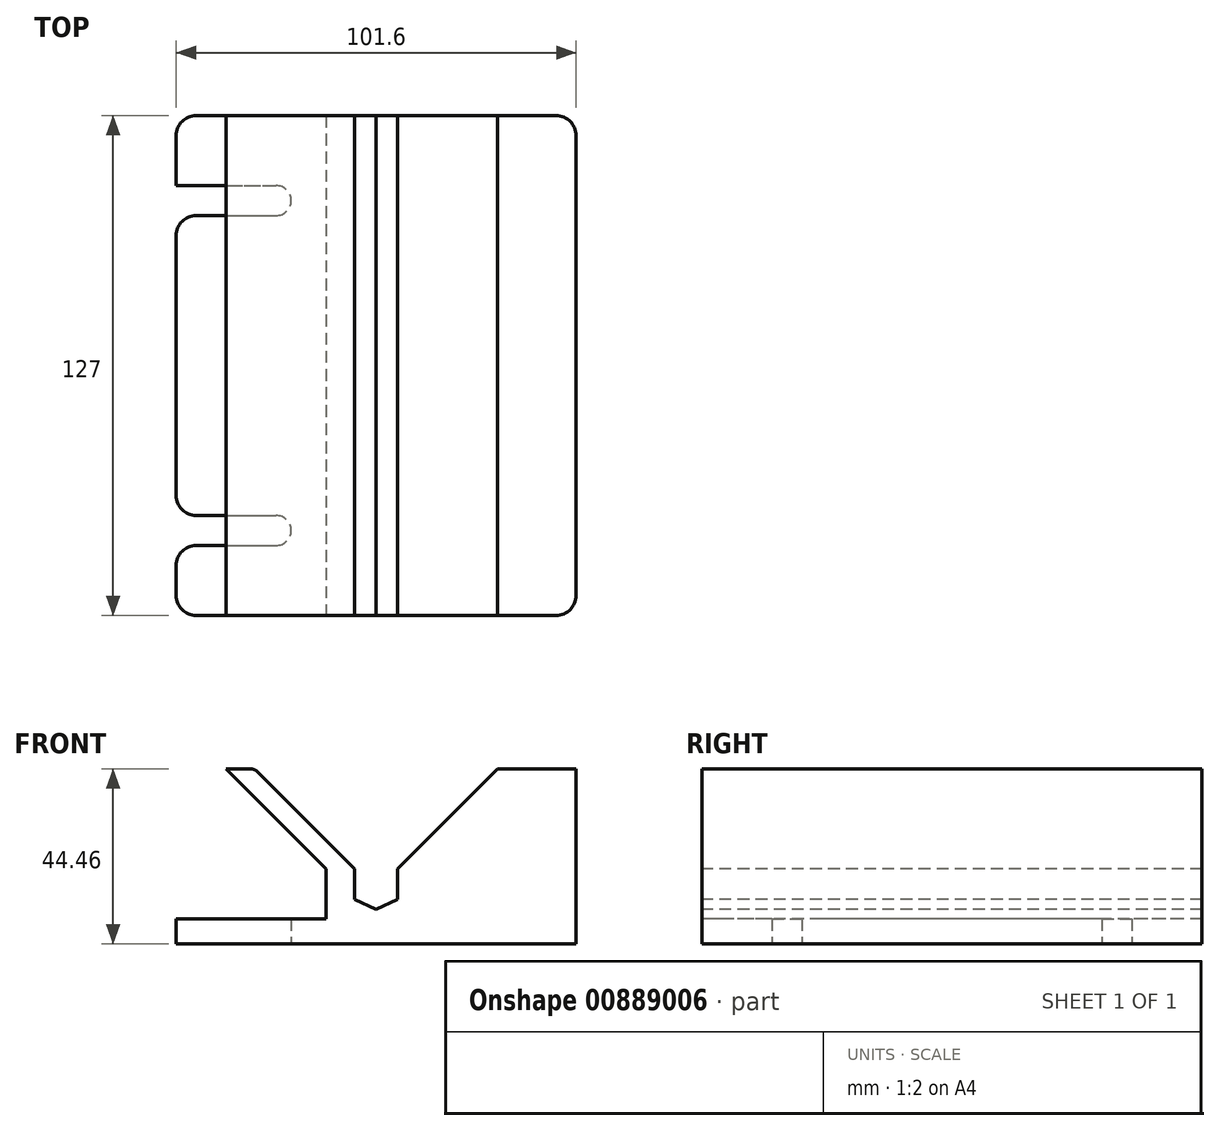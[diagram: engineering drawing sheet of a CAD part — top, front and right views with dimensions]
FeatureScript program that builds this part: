
annotation { "Feature Type Name" : "Feature", "Feature Type Description" : "" }
export const myFeature = defineFeature(function(context is Context, id is Id, definition is map)
    precondition{}
    {
        {
            var Q0;
            Q0=qCreatedBy(makeId("Front.planeOp"),FACE);
            var sketch = newSketch(context, id + "F0", { "sketchPlane" : qUnion([Q0])});
            skLineSegment(sketch, "E0.bottom", {"start": v(50.8, -22.23) * mm, "end": v(-50.8, -22.23) * mm});
            skLineSegment(sketch, "E0.top", {"start": v(50.8, 22.23) * mm, "end": v(-50.8, 22.23) * mm});
            skLineSegment(sketch, "E0.left", {"start": v(50.8, -22.23) * mm, "end": v(50.8, 22.23) * mm});
            skLineSegment(sketch, "E0.right", {"start": v(-50.8, -22.23) * mm, "end": v(-50.8, 22.22) * mm});
            skPoint(sketch, "E0.middle", {"position": v(0, 0) * mm});
            skSolve(sketch);
        }
        {
            var Q0;
            Q0=makeQuery(id+"F0.imprint","IMPRINT",FACE,{"disambiguationData":[TD([[makeQuery(id+"F0.imprint","IMPRINT",EDGE,{"derivedFrom":sQuery(id+"F0.wireOp",EDGE,"E0.bottom")}),-1.0]])]});
            extrude(context, id + "F1", {"entities" : qUnion([Q0]), "endBound" : BoundingType.SYMMETRIC, "depth" : 127 * mm, "offsetDistance" : 25.4 * mm});
        }
        {
            var Q0;
            Q0=makeQuery(id+"F1.opExtrude","CAP_FACE",FACE,{"disambiguationData":[OSD([sQuery(id+"F0.wireOp",EDGE,"E0.bottom"),sQuery(id+"F0.wireOp",EDGE,"E0.top"),sQuery(id+"F0.wireOp",EDGE,"E0.left"),sQuery(id+"F0.wireOp",EDGE,"E0.right")])],"isStart":false});
            var sketch = newSketch(context, id + "F2", { "sketchPlane" : qUnion([Q0])});
            skLineSegment(sketch, "E1", {"start": v(-12.7, -15.88) * mm, "end": v(-50.8, -15.88) * mm});
            skLineSegment(sketch, "E2", {"start": v(-50.8, -15.88) * mm, "end": v(-50.8, 22.22) * mm});
            skLineSegment(sketch, "E3", {"start": v(-50.8, 22.22) * mm, "end": v(-38.1, 22.22) * mm});
            skLineSegment(sketch, "E4", {"start": v(-38.1, 22.23) * mm, "end": v(-12.7, -3.18) * mm});
            skLineSegment(sketch, "E5", {"start": v(-12.7, -3.18) * mm, "end": v(-12.7, -15.88) * mm});
            skSolve(sketch);
        }
        {
            var Q0;
            Q0=makeQuery(id+"F2.imprint","IMPRINT",FACE,{"disambiguationData":[TD([[makeQuery(id+"F2.imprint","IMPRINT",EDGE,{"derivedFrom":sQuery(id+"F2.wireOp",EDGE,"E1")}),-1.0]])]});
            extrude(context, id + "F3", {"entities" : qUnion([Q0]), "operationType" : NewBodyOperationType.REMOVE, "endBound" : BoundingType.THROUGH_ALL, "oppositeDirection" : true, "depth" : 25.4 * mm, "offsetDistance" : 25.4 * mm});
        }
        {
            var Q0;
            Q0=makeQuery(id+"F1.opExtrude","CAP_FACE",FACE,{"disambiguationData":[OSD([sQuery(id+"F0.wireOp",EDGE,"E0.bottom"),sQuery(id+"F0.wireOp",EDGE,"E0.top"),sQuery(id+"F0.wireOp",EDGE,"E0.left"),sQuery(id+"F0.wireOp",EDGE,"E0.right")])],"isStart":false});
            var sketch = newSketch(context, id + "F4", { "sketchPlane" : qUnion([Q0])});
            skLineSegment(sketch, "E6", {"start": v(-30.86, 22.23) * mm, "end": v(-5.46, -3.18) * mm});
            skLineSegment(sketch, "E7", {"start": v(-5.46, -3.18) * mm, "end": v(-5.46, -10.9) * mm});
            skLineSegment(sketch, "E8", {"start": v(-5.46, -10.9) * mm, "end": v(0, -13.45) * mm});
            skLineSegment(sketch, "E9", {"start": v(0, -13.45) * mm, "end": v(5.46, -10.9) * mm});
            skLineSegment(sketch, "E10", {"start": v(5.46, -10.9) * mm, "end": v(5.46, -3.18) * mm});
            skLineSegment(sketch, "E11", {"start": v(5.46, -3.18) * mm, "end": v(30.86, 22.23) * mm});
            skLineSegment(sketch, "E12", {"start": v(30.86, 22.23) * mm, "end": v(-30.86, 22.22) * mm});
            skSolve(sketch);
        }
        {
            var Q0;
            Q0=makeQuery(id+"F4.imprint","IMPRINT",FACE,{"disambiguationData":[TD([[makeQuery(id+"F4.imprint","IMPRINT",EDGE,{"derivedFrom":sQuery(id+"F4.wireOp",EDGE,"E6")}),1.0]])]});
            extrude(context, id + "F5", {"entities" : qUnion([Q0]), "operationType" : NewBodyOperationType.REMOVE, "endBound" : BoundingType.THROUGH_ALL, "oppositeDirection" : true, "depth" : 25.4 * mm, "offsetDistance" : 25.4 * mm});
        }
        {
            var Q0;
            Q0=makeQuery(id+"F3.boolean.opBoolean","COPY",EDGE,{"derivedFrom":makeQuery(id+"F3.opExtrude","SWEPT_EDGE",EDGE,{"disambiguationData":[OSD([sQuery(id+"F0.wireOp",EDGE,"E0.top"),sQuery(id+"F2.wireOp",EDGE,"E3"),sQuery(id+"F2.wireOp",EDGE,"E4")])]})});
            var Q1;
            Q1=makeQuery(id+"F5.boolean.opBoolean","COPY",EDGE,{"derivedFrom":makeQuery(id+"F5.opExtrude","SWEPT_EDGE",EDGE,{"disambiguationData":[OSD([sQuery(id+"F0.wireOp",EDGE,"E0.top"),sQuery(id+"F4.wireOp",EDGE,"E6"),sQuery(id+"F4.wireOp",EDGE,"E12")])]})});
            var Q2;
            Q2=makeQuery(id+"F5.boolean.opBoolean","COPY",EDGE,{"derivedFrom":makeQuery(id+"F5.opExtrude","SWEPT_EDGE",EDGE,{"disambiguationData":[OSD([sQuery(id+"F0.wireOp",EDGE,"E0.top"),sQuery(id+"F4.wireOp",EDGE,"E11"),sQuery(id+"F4.wireOp",EDGE,"E12")])]})});
            var Q3;
            Q3=makeQuery(id+"FReAnOjBeKejbQ6_1.1.F3.boolean.opBoolean","COPY",EDGE,{"derivedFrom":makeQuery(id+"FReAnOjBeKejbQ6_1.1.F3.opExtrude","SWEPT_EDGE",EDGE,{"disambiguationData":[OSD([sQuery(id+"F0.wireOp",EDGE,"E0.top"),sQuery(id+"F2.wireOp",EDGE,"E3"),sQuery(id+"F2.wireOp",EDGE,"E4")])]})});
            fillet(context, id + "F6", {"entities" : qUnion([Q0, Q1, Q2, Q3]), "radius" : 2.54 * mm, "tangentPropagation" : true, "allowEdgeOverflow" : false});
        }
        {
            var Q0;
            Q0=makeQuery(id+"F1.opExtrude","SWEPT_FACE",FACE,{"disambiguationData":[OSD([sQuery(id+"F0.wireOp",EDGE,"E0.bottom")])]});
            var sketch = newSketch(context, id + "F7", { "sketchPlane" : qUnion([Q0])});
            skLineSegment(sketch, "E13.bottom", {"start": v(-50.8, 45.72) * mm, "end": v(-25.4, 45.72) * mm});
            skLineSegment(sketch, "E13.top", {"start": v(-50.8, 38.1) * mm, "end": v(-25.4, 38.1) * mm});
            skLineSegment(sketch, "E13.left", {"start": v(-50.8, 45.72) * mm, "end": v(-50.8, 38.1) * mm});
            skLineSegment(sketch, "E13.right", {"start": v(-25.4, 45.72) * mm, "end": v(-25.4, 38.1) * mm, "construction": true});
            skLineSegment(sketch, "E14.bottom", {"start": v(-50.8, -38.1) * mm, "end": v(-25.4, -38.1) * mm});
            skLineSegment(sketch, "E14.top", {"start": v(-50.8, -45.72) * mm, "end": v(-25.4, -45.72) * mm});
            skLineSegment(sketch, "E14.left", {"start": v(-50.8, -38.1) * mm, "end": v(-50.8, -45.72) * mm});
            skLineSegment(sketch, "E14.right", {"start": v(-25.4, -38.1) * mm, "end": v(-25.4, -45.72) * mm, "construction": true});
            skArc(sketch, "E15", {"start": v(-25.4, 38.1) * mm, "mid": v(-21.59, 41.91) * mm, "end": v(-25.4, 45.72) * mm});
            skArc(sketch, "E16", {"start": v(-25.4, -45.72) * mm, "mid": v(-21.59, -41.9) * mm, "end": v(-25.4, -38.1) * mm});
            skSolve(sketch);
        }
        {
            var Q0;
            Q0=qSketchRegion(id+"F7",true);
            var Q1;
            Q1=makeQuery(id+"F3.boolean.opBoolean","COPY",FACE,{"derivedFrom":makeQuery(id+"F3.opExtrude","SWEPT_FACE",FACE,{"disambiguationData":[OSD([sQuery(id+"F2.wireOp",EDGE,"E1")])]})});
            extrude(context, id + "F8", {"entities" : qUnion([Q0]), "operationType" : NewBodyOperationType.REMOVE, "endBound" : BoundingType.UP_TO_SURFACE, "oppositeDirection" : true, "depth" : 25.4 * mm, "endBoundEntityFace" : qUnion([Q1]), "offsetDistance" : 25.4 * mm});
        }
        {
            var Q0;
            Q0=makeQuery(id+"F1.opExtrude","CAP_EDGE",EDGE,{"disambiguationData":[OSD([sQuery(id+"F0.wireOp",EDGE,"E0.right")])],"isStart":false});
            var Q1;
            Q1=makeQuery(id+"F1.opExtrude","CAP_EDGE",EDGE,{"disambiguationData":[OSD([sQuery(id+"F0.wireOp",EDGE,"E0.right")])],"isStart":true});
            var Q2;
            Q2=makeQuery(id+"F1.opExtrude","CAP_EDGE",EDGE,{"disambiguationData":[OSD([sQuery(id+"F0.wireOp",EDGE,"E0.left")])],"isStart":false});
            var Q3;
            Q3=makeQuery(id+"F1.opExtrude","CAP_EDGE",EDGE,{"disambiguationData":[OSD([sQuery(id+"F0.wireOp",EDGE,"E0.left")])],"isStart":true});
            var Q4;
            Q4=makeQuery(id+"F2x58J9mWKbWmGX_1.1.F8.boolean.opBoolean","COPY",EDGE,{"derivedFrom":makeQuery(id+"F2x58J9mWKbWmGX_1.1.F8.opExtrude","SWEPT_EDGE",EDGE,{"disambiguationData":[OSD([sQuery(id+"F0.wireOp",EDGE,"E0.bottom"),sQuery(id+"F0.wireOp",EDGE,"E0.right"),sQuery(id+"F7.wireOp",EDGE,"E13.bottom"),sQuery(id+"F7.wireOp",EDGE,"E13.left")])]})});
            var Q5;
            Q5=makeQuery(id+"F2x58J9mWKbWmGX_1.1.F8.boolean.opBoolean","COPY",EDGE,{"derivedFrom":makeQuery(id+"F2x58J9mWKbWmGX_1.1.F8.opExtrude","SWEPT_EDGE",EDGE,{"disambiguationData":[OSD([sQuery(id+"F0.wireOp",EDGE,"E0.bottom"),sQuery(id+"F0.wireOp",EDGE,"E0.right"),sQuery(id+"F7.wireOp",EDGE,"E13.top"),sQuery(id+"F7.wireOp",EDGE,"E13.left")])]})});
            var Q6;
            Q6=makeQuery(id+"F2x58J9mWKbWmGX_1.1.F8.boolean.opBoolean","COPY",EDGE,{"derivedFrom":makeQuery(id+"F2x58J9mWKbWmGX_1.1.F8.opExtrude","SWEPT_EDGE",EDGE,{"disambiguationData":[OSD([sQuery(id+"F0.wireOp",EDGE,"E0.bottom"),sQuery(id+"F0.wireOp",EDGE,"E0.right"),sQuery(id+"F7.wireOp",EDGE,"E14.bottom"),sQuery(id+"F7.wireOp",EDGE,"E14.left")])]})});
            var Q7;
            Q7=makeQuery(id+"F2x58J9mWKbWmGX_1.1.F8.boolean.opBoolean","COPY",EDGE,{"derivedFrom":makeQuery(id+"F2x58J9mWKbWmGX_1.1.F8.opExtrude","SWEPT_EDGE",EDGE,{"disambiguationData":[OSD([sQuery(id+"F0.wireOp",EDGE,"E0.bottom"),sQuery(id+"F0.wireOp",EDGE,"E0.right"),sQuery(id+"F7.wireOp",EDGE,"E14.top"),sQuery(id+"F7.wireOp",EDGE,"E14.left")])]})});
            var Q8;
            Q8=makeQuery(id+"F8.boolean.opBoolean","COPY",EDGE,{"derivedFrom":makeQuery(id+"F8.opExtrude","SWEPT_EDGE",EDGE,{"disambiguationData":[OSD([sQuery(id+"F0.wireOp",EDGE,"E0.bottom"),sQuery(id+"F0.wireOp",EDGE,"E0.right"),sQuery(id+"F7.wireOp",EDGE,"E13.bottom"),sQuery(id+"F7.wireOp",EDGE,"E13.left")])]})});
            var Q9;
            Q9=makeQuery(id+"F8.boolean.opBoolean","COPY",EDGE,{"derivedFrom":makeQuery(id+"F8.opExtrude","SWEPT_EDGE",EDGE,{"disambiguationData":[OSD([sQuery(id+"F0.wireOp",EDGE,"E0.bottom"),sQuery(id+"F0.wireOp",EDGE,"E0.right"),sQuery(id+"F7.wireOp",EDGE,"E14.bottom"),sQuery(id+"F7.wireOp",EDGE,"E14.left")])]})});
            var Q10;
            Q10=makeQuery(id+"F8.boolean.opBoolean","COPY",EDGE,{"derivedFrom":makeQuery(id+"F8.opExtrude","SWEPT_EDGE",EDGE,{"disambiguationData":[OSD([sQuery(id+"F0.wireOp",EDGE,"E0.bottom"),sQuery(id+"F0.wireOp",EDGE,"E0.right"),sQuery(id+"F7.wireOp",EDGE,"E14.top"),sQuery(id+"F7.wireOp",EDGE,"E14.left")])]})});
            var Q11;
            Q11=makeQuery(id+"F8.boolean.opBoolean","COPY",EDGE,{"derivedFrom":makeQuery(id+"F8.opExtrude","SWEPT_EDGE",EDGE,{"disambiguationData":[OSD([sQuery(id+"F0.wireOp",EDGE,"E0.bottom"),sQuery(id+"F0.wireOp",EDGE,"E0.right"),sQuery(id+"F7.wireOp",EDGE,"E13.top"),sQuery(id+"F7.wireOp",EDGE,"E13.left")])]})});
            fillet(context, id + "F9", {"entities" : qUnion([Q0, Q1, Q2, Q3, Q4, Q5, Q6, Q7, Q8, Q9, Q10, Q11]), "radius" : 5.08 * mm, "tangentPropagation" : true, "allowEdgeOverflow" : false});
        }
    });
